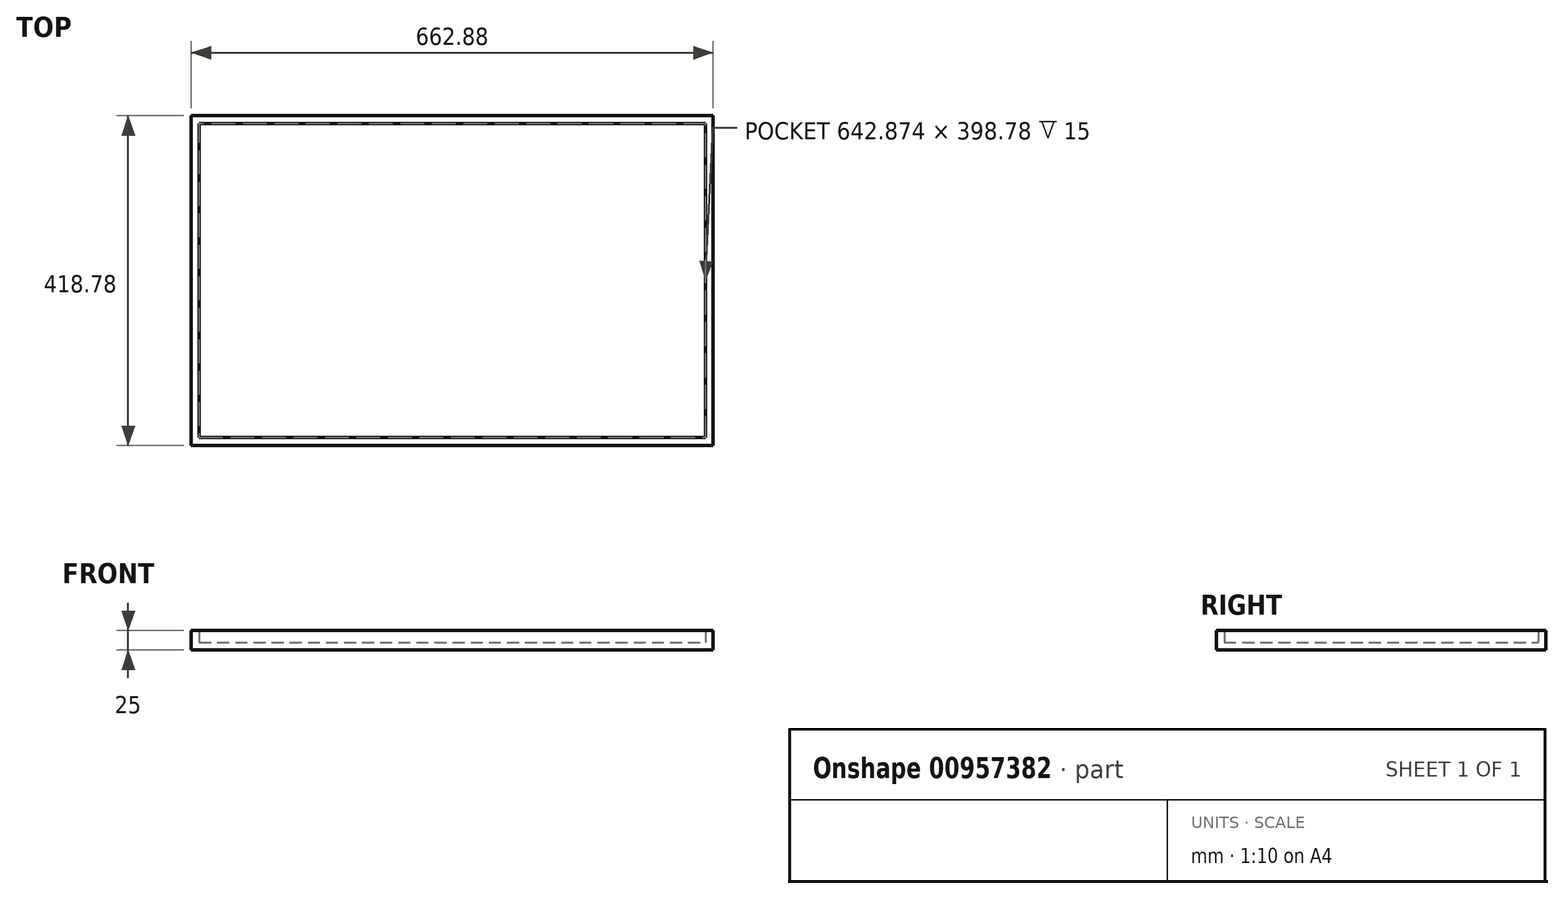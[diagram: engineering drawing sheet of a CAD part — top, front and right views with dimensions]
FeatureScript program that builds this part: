
annotation { "Feature Type Name" : "Feature", "Feature Type Description" : "" }
export const myFeature = defineFeature(function(context is Context, id is Id, definition is map)
    precondition{}
    {
        {
            var Q0;
            Q0=qCreatedBy(makeId("Top.planeOp"),FACE);
            var sketch = newSketch(context, id + "F0", { "sketchPlane" : qUnion([Q0])});
            skLineSegment(sketch, "E0.bottom", {"start": v(321.44, 199.4) * mm, "end": v(-321.44, 199.39) * mm});
            skLineSegment(sketch, "E0.top", {"start": v(321.44, -199.39) * mm, "end": v(-321.44, -199.39) * mm});
            skLineSegment(sketch, "E0.left", {"start": v(321.44, 199.4) * mm, "end": v(321.44, -199.39) * mm});
            skLineSegment(sketch, "E0.right", {"start": v(-321.44, 199.4) * mm, "end": v(-321.44, -199.39) * mm});
            skPoint(sketch, "E0.middle", {"position": v(0, 0) * mm});
            skLineSegment(sketch, "E1.bottom", {"start": v(331.44, -209.39) * mm, "end": v(-331.44, -209.4) * mm});
            skLineSegment(sketch, "E1.top", {"start": v(331.44, 209.4) * mm, "end": v(-331.44, 209.39) * mm});
            skLineSegment(sketch, "E1.left", {"start": v(331.44, -209.39) * mm, "end": v(331.44, 209.4) * mm});
            skLineSegment(sketch, "E1.right", {"start": v(-331.44, -209.4) * mm, "end": v(-331.44, 209.39) * mm});
            skSolve(sketch);
        }
        {
            var Q0;
            Q0 = qSketchRegion(id + "F0", true);
            var Q1;
            Q1=makeQuery(id+"F0.imprint","IMPRINT",FACE,{"disambiguationData":[TD([[makeQuery(id+"F0.imprint","IMPRINT",EDGE,{"derivedFrom":sQuery(id+"F0.wireOp",EDGE,"E0.bottom")}),1.0]])]});
            extrude(context, id + "F1", {"entities" : qUnion([Q0, Q1]), "depth" : 10 * mm, "offsetDistance" : 25 * mm});
        }
        {
            var Q0;
            Q0 = qSketchRegion(id + "F0", true);
            extrude(context, id + "F2", {"entities" : qUnion([Q0]), "operationType" : NewBodyOperationType.ADD, "depth" : 25 * mm, "offsetDistance" : 25 * mm});
        }
    });
